# Revit family: FP_Revit_18_HT90GCX1_Rangehood_90001898A
name_source: partatom
category: Specialty Equipment
revit_build: Autodesk Revit 2018 (Build: 20170223_1515(x64)
units: mm (PartAtom-declared; Revit-internal decimal feet)

## family parameters
Always vertical = Yes
Cut with Voids When Loaded = Yes
OmniClass Number = 23.40.40.00
OmniClass Title = Food Service Equipment and Furnishings
Part Type = Normal
Room Calculation Point = No
Round Connector Dimension = Use Diameter
Shared = No
Work Plane-Based = No

## types (2) — shared parameters
Chassis - Depth = 328 mm  [stored 1.07612 ft]
Chassis - Height = 635 mm
Chassis - Width = 407 mm  [stored 1.3353 ft]
Connector Description - Electrical = 220 V, 50 Hz,  222 W
Connector Description - Extraction = 180mm Semi Rigid Rangehood Ducting, 650Pa
Description = 90cm Rangehood
Manufacturer = Fisher & Paykel Appliances
Material - Body = Fisher & Paykel - Stainless Steel
Material - Glass = Fisher & Paykel - Black
Model = HT90GCX1
Product - Depth = 531 mm  [stored 1.74213 ft]
Product - Width = 900 mm  [stored 2.95276 ft]
URL = www.fisherpaykel.com

## per-type parameters (varying)
| type | Visibility - Door Closed | Visibility - Door Open |
| HT90GCX1 (Door Open) | No | Yes |
| HT90GCX1 (Door Closed) | Yes | No |

note: [stored X ft] marks values corroborated as IEEE doubles in the binary element streams (Revit-internal decimal feet)

## geometry (parser evidence)
native form markers: Sweep x2
no freeform markers — native parametric forms only
